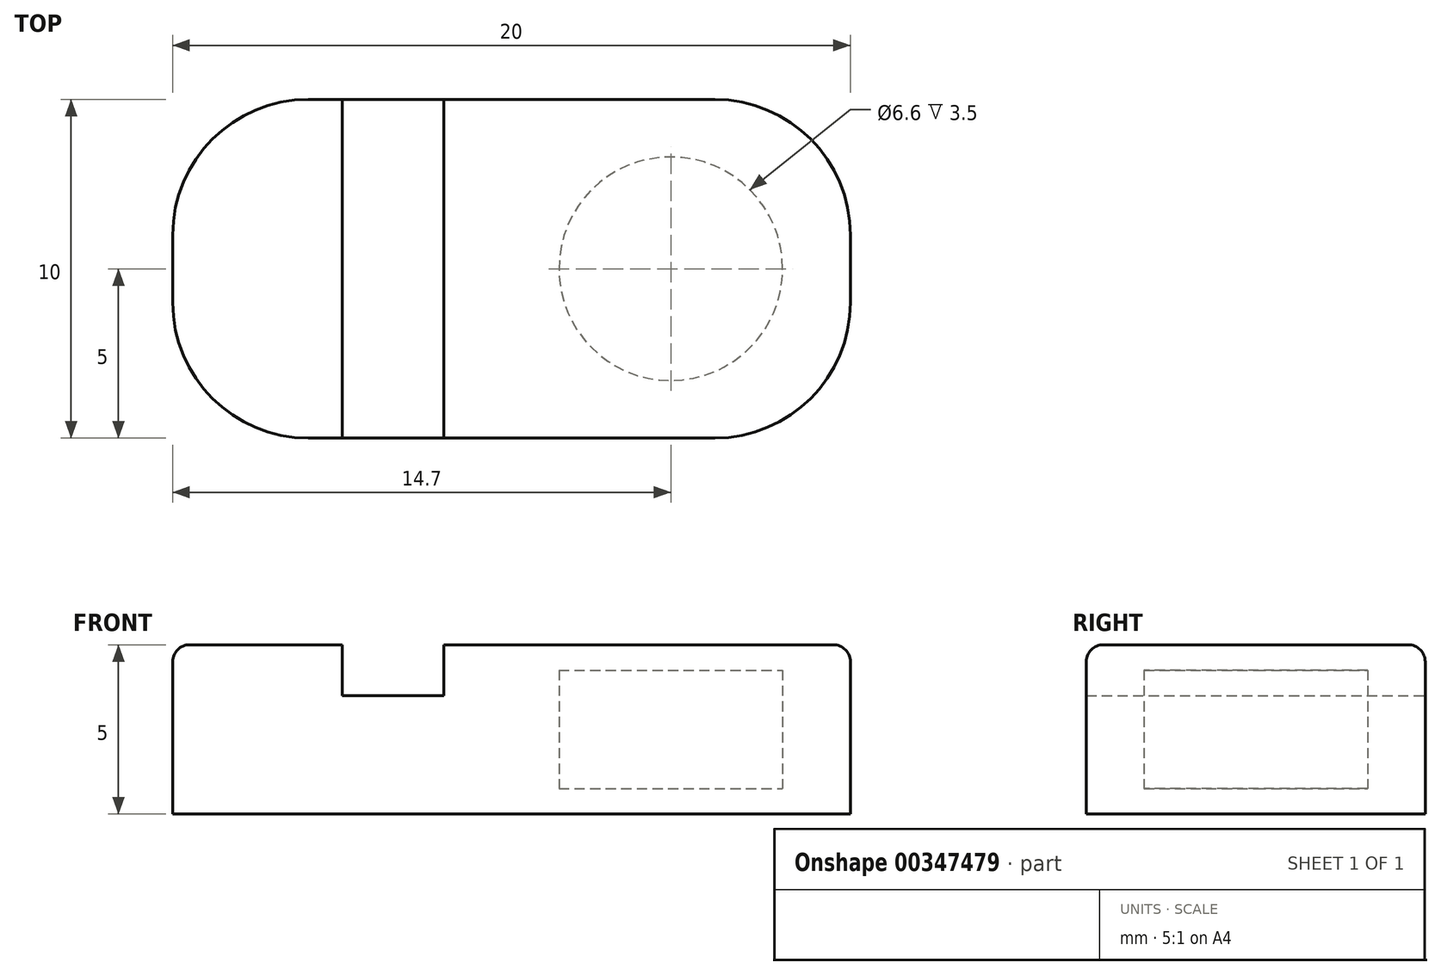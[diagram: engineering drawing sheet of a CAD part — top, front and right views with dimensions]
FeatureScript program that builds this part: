
annotation { "Feature Type Name" : "Feature", "Feature Type Description" : "" }
export const myFeature = defineFeature(function(context is Context, id is Id, definition is map)
    precondition{}
    {
        {
            var Q0;
            Q0=qCreatedBy(makeId("Top.planeOp"),FACE);
            var sketch = newSketch(context, id + "F0", { "sketchPlane" : qUnion([Q0])});
            skLineSegment(sketch, "E0.bottom", {"start": v(6, -5) * mm, "end": v(-6, -5) * mm});
            skLineSegment(sketch, "E0.top", {"start": v(6, 5) * mm, "end": v(-6, 5) * mm});
            skLineSegment(sketch, "E0.left", {"start": v(10, -1) * mm, "end": v(10, 1) * mm});
            skLineSegment(sketch, "E0.right", {"start": v(-10, -1) * mm, "end": v(-10, 1) * mm});
            skPoint(sketch, "E0.middle", {"position": v(0, 0) * mm});
            skPoint(sketch, "E1.visualSharp", {"position": v(-10, 5) * mm});
            skArc(sketch, "E1.filletArc", {"start": v(-6, 5) * mm, "mid": v(-8.83, 3.83) * mm, "end": v(-10, 1) * mm});
            skPoint(sketch, "E2.visualSharp", {"position": v(-10, -5) * mm});
            skArc(sketch, "E2.filletArc", {"start": v(-10, -1) * mm, "mid": v(-8.83, -3.83) * mm, "end": v(-6, -5) * mm});
            skPoint(sketch, "E3.visualSharp", {"position": v(10, -5) * mm});
            skArc(sketch, "E3.filletArc", {"start": v(6, -5) * mm, "mid": v(8.83, -3.83) * mm, "end": v(10, -1) * mm});
            skPoint(sketch, "E4.visualSharp", {"position": v(10, 5) * mm});
            skArc(sketch, "E4.filletArc", {"start": v(10, 1) * mm, "mid": v(8.83, 3.83) * mm, "end": v(6, 5) * mm});
            skSolve(sketch);
        }
        {
            var Q0;
            Q0=makeQuery(id+"F0.imprint","IMPRINT",FACE,{"disambiguationData":[TD([[makeQuery(id+"F0.imprint","IMPRINT",EDGE,{"derivedFrom":sQuery(id+"F0.wireOp",EDGE,"E0.bottom")}),-1.0]])]});
            extrude(context, id + "F1", {"entities" : qUnion([Q0]), "depth" : 5 * mm});
        }
        {
            var Q0;
            Q0=makeQuery(id+"F1.opExtrude","CAP_FACE",FACE,{"disambiguationData":[OSD([sQuery(id+"F0.wireOp",EDGE,"E0.bottom"),sQuery(id+"F0.wireOp",EDGE,"E0.top"),sQuery(id+"F0.wireOp",EDGE,"E0.left"),sQuery(id+"F0.wireOp",EDGE,"E0.right")])],"isStart":false});
            var sketch = newSketch(context, id + "F2", { "sketchPlane" : qUnion([Q0])});
            skLineSegment(sketch, "E5.bottom", {"start": v(-2, -5) * mm, "end": v(-5, -5) * mm});
            skLineSegment(sketch, "E5.top", {"start": v(-2, 5) * mm, "end": v(-5, 5) * mm});
            skLineSegment(sketch, "E5.left", {"start": v(-2, -5) * mm, "end": v(-2, 5) * mm});
            skLineSegment(sketch, "E5.right", {"start": v(-5, -5) * mm, "end": v(-5, 5) * mm});
            skPoint(sketch, "E5.middle", {"position": v(-3.5, 0) * mm});
            skSolve(sketch);
        }
        {
            var Q0;
            Q0 = qSketchRegion(id + "F2", true);
            extrude(context, id + "F3", {"entities" : qUnion([Q0]), "operationType" : NewBodyOperationType.REMOVE, "oppositeDirection" : true, "depth" : 1.5 * mm});
        }
        {
            var Q0;
            Q0=makeQuery(id+"F3.boolean.opBoolean","COPY",EDGE,{"derivedFrom":makeQuery(id+"F3.opExtrude","CAP_EDGE",EDGE,{"disambiguationData":[OSD([sQuery(id+"F2.wireOp",EDGE,"E5.bottom")])],"isStart":false})});
            var Q1;
            Q1=makeQuery(id+"F3.boolean.opBoolean","COPY",EDGE,{"derivedFrom":makeQuery(id+"F3.opExtrude","CAP_EDGE",EDGE,{"disambiguationData":[OSD([sQuery(id+"F2.wireOp",EDGE,"03266f9c-a140-4e30-9566-a50e59f9c8991.MirrorCS")])],"isStart":false})});
            var Q2;
            Q2=makeQuery(id+"F3.boolean.opBoolean","COPY",EDGE,{"derivedFrom":makeQuery(id+"F3.opExtrude","CAP_EDGE",EDGE,{"disambiguationData":[OSD([sQuery(id+"F2.wireOp",EDGE,"03266f9c-a140-4e30-9566-a50e59f9c8994.MirrorCS")])],"isStart":false})});
            var Q3;
            Q3=makeQuery(id+"F3.boolean.opBoolean","COPY",EDGE,{"derivedFrom":makeQuery(id+"F3.opExtrude","CAP_EDGE",EDGE,{"disambiguationData":[OSD([sQuery(id+"F2.wireOp",EDGE,"E5.top")])],"isStart":false})});
            var Q4;
            Q4=makeQuery(id+"F1.opExtrude","CAP_EDGE",EDGE,{"disambiguationData":[OSD([sQuery(id+"F0.wireOp",EDGE,"E0.top")])],"isStart":false});
            var Q5;
            Q5=makeQuery(id+"F1.opExtrude","CAP_EDGE",EDGE,{"disambiguationData":[OSD([sQuery(id+"F0.wireOp",EDGE,"E0.bottom")])],"isStart":false});
            fillet(context, id + "F4", {"entities" : qUnion([Q0, Q1, Q2, Q3, Q4, Q5]), "radius" : .5 * mm, "tangentPropagation" : true, "allowEdgeOverflow" : false});
        }
        {
            var Q0;
            Q0=makeQuery(id+"F1.opExtrude","CAP_FACE",FACE,{"disambiguationData":[OSD([sQuery(id+"F0.wireOp",EDGE,"E0.bottom"),sQuery(id+"F0.wireOp",EDGE,"E0.top"),sQuery(id+"F0.wireOp",EDGE,"E0.left"),sQuery(id+"F0.wireOp",EDGE,"E0.right"),sQuery(id+"F0.wireOp",EDGE,"E1.filletArc"),sQuery(id+"F0.wireOp",EDGE,"E2.filletArc"),sQuery(id+"F0.wireOp",EDGE,"E3.filletArc"),sQuery(id+"F0.wireOp",EDGE,"E4.filletArc")])],"isStart":true});
            var sketch = newSketch(context, id + "F5", { "sketchPlane" : qUnion([Q0])});
            skCircle(sketch, "E6", {"center": v(4.7, 0) * mm, "radius": 3.3 * mm});
            skSolve(sketch);
        }
        {
            var Q0;
            Q0=makeQuery(id+"F5.imprint","IMPRINT",FACE,{"disambiguationData":[TD([[makeQuery(id+"F5.imprint","IMPRINT",EDGE,{"derivedFrom":sQuery(id+"F5.wireOp",EDGE,"E6")}),1.0]])]});
            extrude(context, id + "F6", {"entities" : qUnion([Q0]), "operationType" : NewBodyOperationType.REMOVE, "oppositeDirection" : true, "depth" : 4.25 * mm, "hasSecondDirection" : true, "secondDirectionOppositeDirection" : true, "secondDirectionDepth" : .75 * mm});
        }
    });
